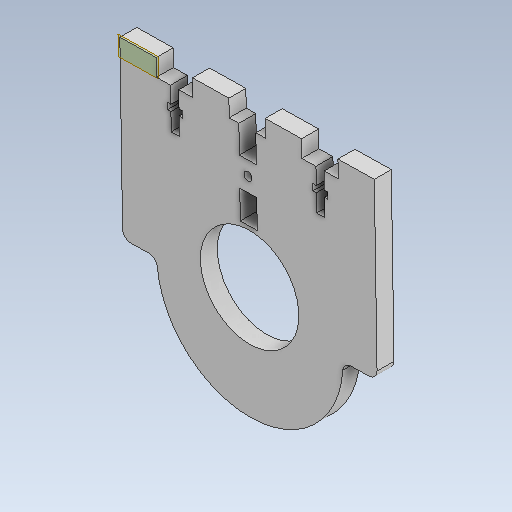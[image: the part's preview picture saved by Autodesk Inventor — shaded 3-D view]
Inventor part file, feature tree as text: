
AUTODESK INVENTOR PART (.ipt)
format: ipt  version: 2021.1 (Build 251245010, 245A)  size: 214,016 bytes
history: native  units: mm
features: reference x25, other x7, extrude x2, sketch x2
ambient origin geometry x8: Origin, YZ Plane, XZ Plane, XY Plane, X Axis, Y Axis, Z Axis, Center Point
bodies: Body1 (feature_tree)
feature tree (36):
  other  "Твердое тело1"
  other  "РабПлоскость1"
  extrude  "Выдавливание1"  Depth=6.2mm
  extrude  "Выдавливание2"  Depth=6.2mm
  sketch  "Эскиз1"
  reference  "Ссылка1"
  reference  "Ссылка2"
  reference  "Ссылка3"
  reference  "Ссылка4"
  reference  "Ссылка5"
  reference  "Ссылка6"
  reference  "Ссылка9"
  reference  "Ссылка10"
  reference  "Ссылка13"
  reference  "Ссылка14"
  reference  "Ссылка17"
  reference  "Ссылка18"
  reference  "Ссылка19"
  reference  "Ссылка20"
  reference  "Ссылка21"
  reference  "Ссылка22"
  sketch  "Эскиз2"
  reference  "Ссылка36"
  reference  "Ссылка60"
  reference  "Ссылка61"
  reference  "Ссылка62"
  reference  "Ссылка63"
  reference  "Ссылка65"
  reference  "Ссылка67"
  reference  "Ссылка68"
  reference  "Ссылка70"
  other  "<userpath>\Documents\Savka\3d\Korp.iam"
  other  "Korp.iam"
  other  "Korpus 5:1"
  other  "Korpus 3:1"
  other  "44260_txm torquenado dc motor:1"
